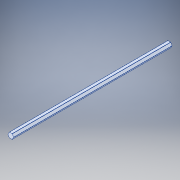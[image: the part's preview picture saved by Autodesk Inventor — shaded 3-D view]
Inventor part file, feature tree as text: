
AUTODESK INVENTOR PART (.ipt)
format: ipt  version: 2017 (Build 210142000, 142)  size: 154,624 bytes
history: native  units: in
note: dims shown in document units (in); Inventor stores cm internally (conversion verified against a paired STEP export)
features: sketch x6, split x1, fillet x1
ambient origin geometry x8: Origin, YZ Plane, XZ Plane, XY Plane, X Axis, Y Axis, Z Axis, Center Point
bodies: Solid1 (feature_tree)
feature tree (8):
  sketch  "Sketch1"  dims[d11=16.0in]
  split  "Split1"
  sketch  "Sketch3"  dims[d13=7.8125in]
  sketch  "Sketch4"  dims[d14=3.5453in]
  sketch  "Sketch5"  dims[d15=3.5453in]
  sketch  "Sketch7"
  sketch  "Sketch2"  dims[d12=7.8125in]
  fillet  "Fillet1"  Radius=8.5in
